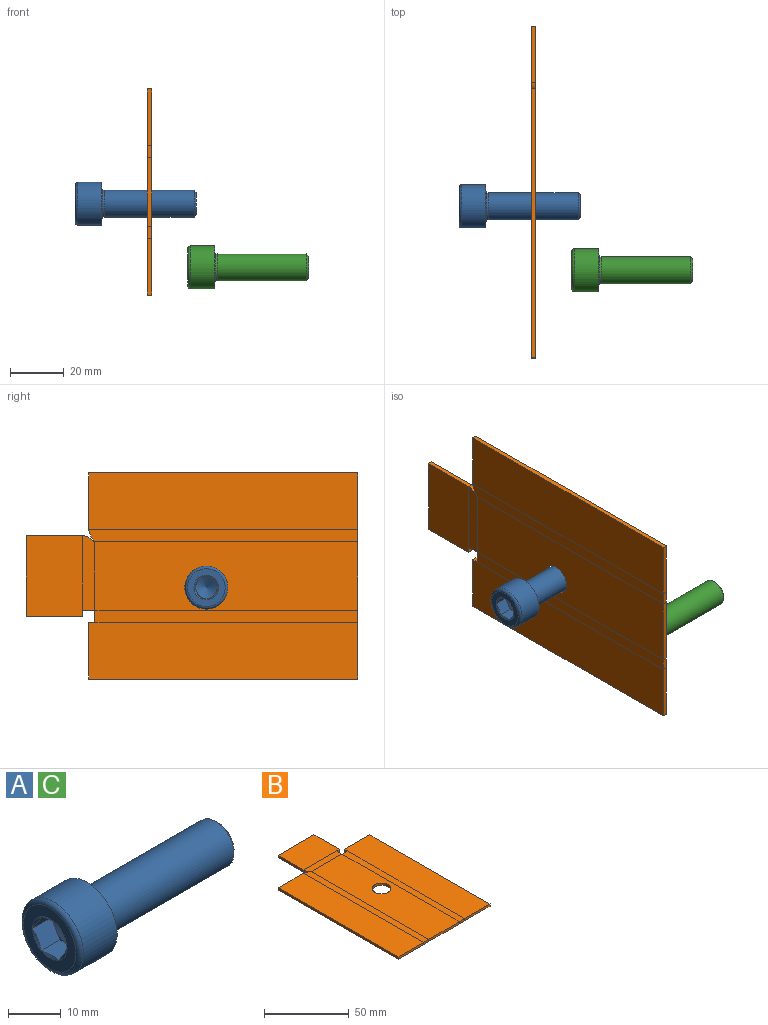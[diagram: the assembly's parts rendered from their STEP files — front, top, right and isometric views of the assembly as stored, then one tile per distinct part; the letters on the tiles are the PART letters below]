
ASSEMBLY  parts=3 mates=1
PART A: 29 faces, bbox 45x17.3x17.3 mm
  f0: plane 3.46x2mm, normal (-1,0,0), area 0.9mm2, adj f21,f22,f28
  f1: plane 4x1.15mm, normal (-1,0,0), area 0.9mm2, adj f22,f23,f28
  f2: plane 3.46x2mm, normal (-1,0,0), area 0.9mm2, adj f23,f24,f28
  f3: plane 3.46x2mm, normal (-1,0,0), area 0.9mm2, adj f24,f25,f28
  f4: plane 4x1.15mm, normal (-1,0,0), area 0.9mm2, adj f25,f26,f28
  f5: cone r=4.59mm half-angle=60deg, axis (-1,0,0), area 2.1mm2, adj f11,f21
  f6: cone r=4.59mm half-angle=60deg, axis (-1,0,0), area 2.1mm2, adj f11,f22
  f7: cone r=4.59mm half-angle=60deg, axis (-1,0,0), area 2.1mm2, adj f11,f23
  f8: cone r=4.59mm half-angle=60deg, axis (-1,0,0), area 2.1mm2, adj f11,f24
  f9: cone r=4.59mm half-angle=60deg, axis (-1,0,0), area 2.1mm2, adj f11,f25
  f10: cone r=4.59mm half-angle=60deg, axis (-1,0,0), area 2.1mm2, adj f11,f26
  f11: plane 14x14mm, normal (-1,0,0), area 87.6mm2, adj f5,f6,f7,f8,f9,f10,f20,f21
  f12: cone r=5.02mm half-angle=17.9deg, axis (-1,0,0), area 21mm2, adj f13,f17
  f13: torus R=5.4mm, axis (1,0,0), area 3.9mm2, adj f12,f16
  f14: plane 8.47x8.47mm, normal (1,0,0), area 56.3mm2, adj f15
  f15: cone r=5mm half-angle=45deg, axis (-1,0,0), area 31.5mm2, adj f14,f16
  f16: cylinder r=5mm len=33.21mm, axis (1,0,0), area 1043.4mm2, adj f13,f15
  f17: torus R=5.6mm, axis (1,0,0), area 17mm2, adj f12,f19
  f18: cylinder r=8mm len=16mm, axis (1,0,0), area 452.4mm2, adj f19,f20
  f19: plane 16x16mm, normal (1,0,0), area 102.5mm2, adj f17,f18
  f20: torus R=7mm, axis (1,0,0), area 75.4mm2, adj f11,f18
  f21: plane 5x4.62mm, normal (0,0,-1), area 22.1mm2, adj f0,f5,f11,f22,f26,f27
  f22: plane 5x4mm, normal (0,0.87,-0.5), area 22.1mm2, adj f0,f1,f6,f11,f21,f23
  f23: plane 5x4mm, normal (0,0.87,0.5), area 22.1mm2, adj f1,f2,f7,f11,f22,f24
  f24: plane 5x4.62mm, normal (0,0,1), area 22.1mm2, adj f2,f3,f8,f11,f23,f25
  f25: plane 5x4mm, normal (0,-0.87,0.5), area 22.1mm2, adj f3,f4,f9,f11,f24,f26
  f26: plane 5x4mm, normal (0,-0.87,-0.5), area 22.1mm2, adj f4,f10,f11,f21,f25,f27
  f27: plane 3.46x2mm, normal (-1,0,0), area 0.9mm2, adj f21,f26,f28
  f28: cone r=4mm half-angle=60deg, axis (-1,0,0), area 58mm2, adj f0,f1,f2,f3,f4,f27
PART B: 34 faces, bbox 76.6x123.3x1.6 mm
  f0: plane 25.4x1.6mm, normal (0,-1,0), area 40.6mm2, adj f2,f3,f22,f31
  f1: cylinder r=5.5mm len=11mm, axis (0,0,1), area 55.3mm2, adj f2,f3
  f2: plane 97.7x25.4mm, normal (0,0,-1), area 2386.5mm2, adj f0,f1,f4,f13,f23,f32
  f3: plane 97.7x25.4mm, normal (0,0,1), area 2386.5mm2, adj f0,f1,f4,f14,f24,f33
  f4: plane 1.6x0.01mm, normal (-0.71,0.71,0), area 0mm2, adj f2,f3,f12,f30
  f5: plane 2.28x1.6mm, normal (0,-1,0), area 3.6mm2, adj f7,f9,f10,f11
  f6: plane 29.96x1.6mm, normal (0,1,0), area 47.9mm2, adj f7,f8,f9,f10
  f7: plane 21.1x1.6mm, normal (1,0,0), area 33.8mm2, adj f5,f6,f9,f10
  f8: plane 21.1x1.6mm, normal (-1,0,0), area 33.8mm2, adj f6,f9,f10,f12
  f9: plane 29.96x21.1mm, normal (0,0,-1), area 632.2mm2, adj f5,f6,f7,f8,f13
  f10: plane 29.96x21.1mm, normal (0,0,1), area 632.2mm2, adj f5,f6,f7,f8,f14
  f11: plane 4.49x1.6mm, normal (1,0,0), area 7.2mm2, adj f5,f13,f14,f21
  f12: extruded ~4.49x2.29mm, area 8.2mm2, adj f4,f8,f13,f14
  f13: plane 27.68x4.49mm, normal (0,0,-1), area 120.6mm2, adj f2,f9,f11,f12
  f14: plane 27.68x4.49mm, normal (0,0,1), area 120.6mm2, adj f3,f10,f11,f12
  f15: plane 99.98x1.6mm, normal (1,0,0), area 160mm2, adj f16,f18,f19,f20
  f16: plane 21.1x1.6mm, normal (0,-1,0), area 33.8mm2, adj f15,f19,f20,f22
  f17: plane 2.28x1.6mm, normal (-1,0,0), area 3.6mm2, adj f18,f19,f20,f21
  f18: plane 21.1x1.6mm, normal (0,1,0), area 33.8mm2, adj f15,f17,f19,f20
  f19: plane 99.98x21.1mm, normal (0,0,-1), area 2109.6mm2, adj f15,f16,f17,f18,f23
  f20: plane 99.98x21.1mm, normal (0,0,1), area 2109.6mm2, adj f15,f16,f17,f18,f24
  f21: plane 4.49x1.6mm, normal (0,1,0), area 7.2mm2, adj f11,f17,f23,f24
  f22: plane 4.49x1.6mm, normal (0,-1,0), area 7.2mm2, adj f0,f16,f23,f24
  f23: plane 97.7x4.49mm, normal (0,0,-1), area 438.9mm2, adj f2,f19,f21,f22
  f24: plane 97.7x4.49mm, normal (0,0,1), area 438.9mm2, adj f3,f20,f21,f22
  f25: plane 99.98x1.6mm, normal (-1,0,0), area 160mm2, adj f26,f27,f28,f29
  f26: plane 21.1x1.6mm, normal (0,1,0), area 33.8mm2, adj f25,f28,f29,f30
  f27: plane 21.1x1.6mm, normal (0,-1,0), area 33.8mm2, adj f25,f28,f29,f31
  f28: plane 99.98x21.1mm, normal (0,0,-1), area 2109.6mm2, adj f25,f26,f27,f32
  f29: plane 99.98x21.1mm, normal (0,0,1), area 2109.6mm2, adj f25,f26,f27,f33
  f30: extruded ~4.49x2.29mm, area 8.2mm2, adj f4,f26,f32,f33
  f31: plane 4.49x1.6mm, normal (0,-1,0), area 7.2mm2, adj f0,f27,f32,f33
  f32: plane 99.98x4.49mm, normal (0,0,-1), area 445.4mm2, adj f2,f28,f30,f31
  f33: plane 99.98x4.49mm, normal (0,0,1), area 445.4mm2, adj f3,f29,f30,f31
PART C: same geometry as A
PLACE A t=(42.81,77.97,21.09)mm
PLACE B rot(axis=(0,1,0),90deg) t=(61.24,10.87,32.02)mm
PLACE C t=(84.72,54.24,-2.65)mm
MATE cylindrical B.f1 <-> A.f5  axis (1,0,0) through (60.44,77.97,21.09)mm
